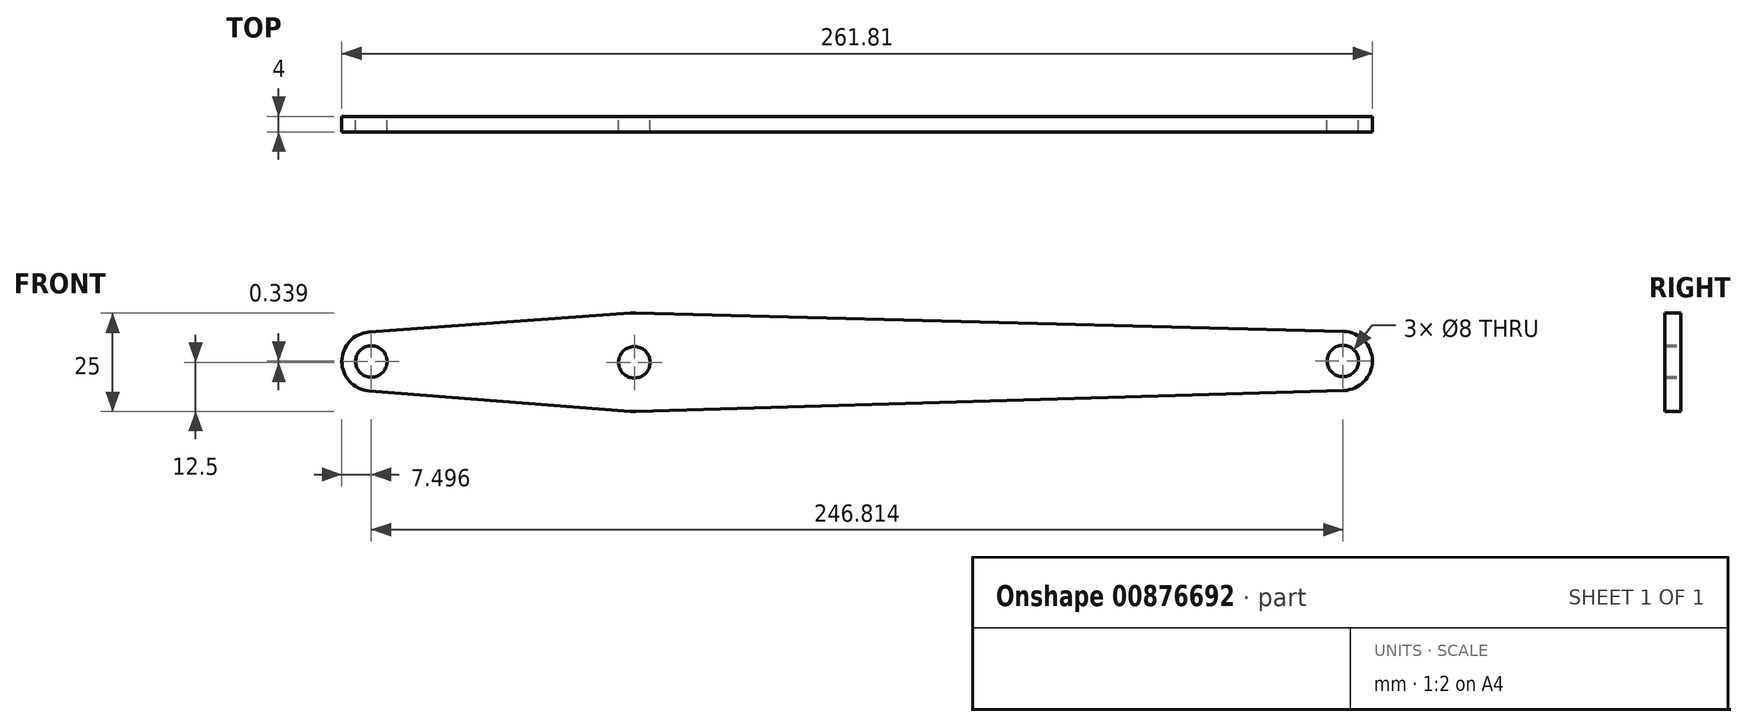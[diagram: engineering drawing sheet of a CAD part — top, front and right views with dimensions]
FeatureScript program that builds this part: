
annotation { "Feature Type Name" : "Feature", "Feature Type Description" : "" }
export const myFeature = defineFeature(function(context is Context, id is Id, definition is map)
    precondition{}
    {
        {
            var Q0;
            Q0=qCreatedBy(makeId("Front.planeOp"),FACE);
            var sketch = newSketch(context, id + "F0", { "sketchPlane" : qUnion([Q0])});
            skCircle(sketch, "E0", {"center": v(0, 0) * mm, "radius": 4 * mm});
            skCircle(sketch, "E1", {"center": v(-66.81, 0.22) * mm, "radius": 4 * mm});
            skCircle(sketch, "E2", {"center": v(180, 0.34) * mm, "radius": 4 * mm});
            skArc(sketch, "E3", {"start": v(-67.35, 7.7) * mm, "mid": v(-74.31, 0.25) * mm, "end": v(-67.4, -7.26) * mm});
            skArc(sketch, "E4", {"start": v(-0.98, -12.46) * mm, "mid": v(-0.3, -12.5) * mm, "end": v(0.37, -12.5) * mm});
            skArc(sketch, "E5", {"start": v(180.22, -7.16) * mm, "mid": v(187.5, 0.35) * mm, "end": v(180.2, 7.84) * mm});
            skLineSegment(sketch, "E6", {"start": v(-0.3, -12.51) * mm, "end": v(180.22, -7.16) * mm});
            skLineSegment(sketch, "E7", {"start": v(-67.4, -7.26) * mm, "end": v(-0.3, -12.51) * mm});
            skLineSegment(sketch, "E8", {"start": v(-67.35, 7.7) * mm, "end": v(-0.9, 12.47) * mm});
            skLineSegment(sketch, "E9", {"start": v(0.32, 12.5) * mm, "end": v(180.2, 7.84) * mm});
            skArc(sketch, "E10.trimOffspring", {"start": v(0.32, 12.5) * mm, "mid": v(-0.29, 12.5) * mm, "end": v(-0.9, 12.47) * mm});
            skSolve(sketch);
        }
        {
            var Q0;
            Q0=makeQuery(id+"F0.imprint","IMPRINT",FACE,{"disambiguationData":[TD([[makeQuery(id+"F0.imprint","IMPRINT",EDGE,{"derivedFrom":sQuery(id+"F0.wireOp",EDGE,"E0")}),-1.0]])]});
            extrude(context, id + "F1", {"entities" : qUnion([Q0]), "depth" : 4 * mm, "offsetDistance" : 25 * mm});
        }
    });
